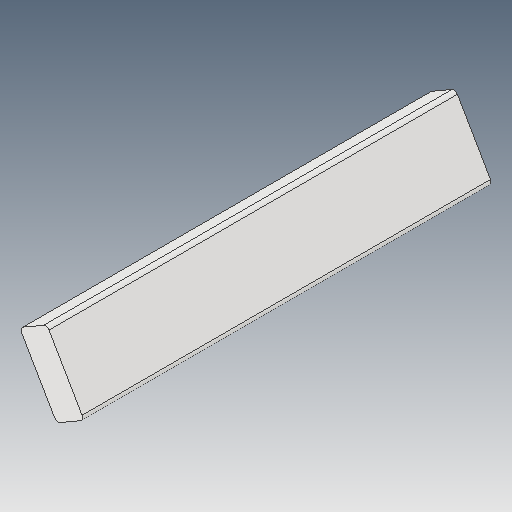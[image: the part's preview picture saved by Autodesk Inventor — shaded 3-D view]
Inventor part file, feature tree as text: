
AUTODESK INVENTOR PART (.ipt)
format: ipt  version: 2023.5 (Build 275446000, 446)  size: 88,576 bytes
history: native  units: in
note: dims shown in document units (in); Inventor stores cm internally (conversion verified against a paired STEP export)
features: fillet x1
ambient origin geometry x8: Origin, YZ Plane, XZ Plane, XY Plane, X Axis, Y Axis, Z Axis, Center Point
bodies: Solid1 (feature_tree)
feature tree (1):
  fillet  "Fillet1"  [1 undecoded]
note: 1 required parameter value undecoded (feature->parameter linkage not recoverable at this tier; creation-order binding heuristic only, values carry confidence <= 0.55)
